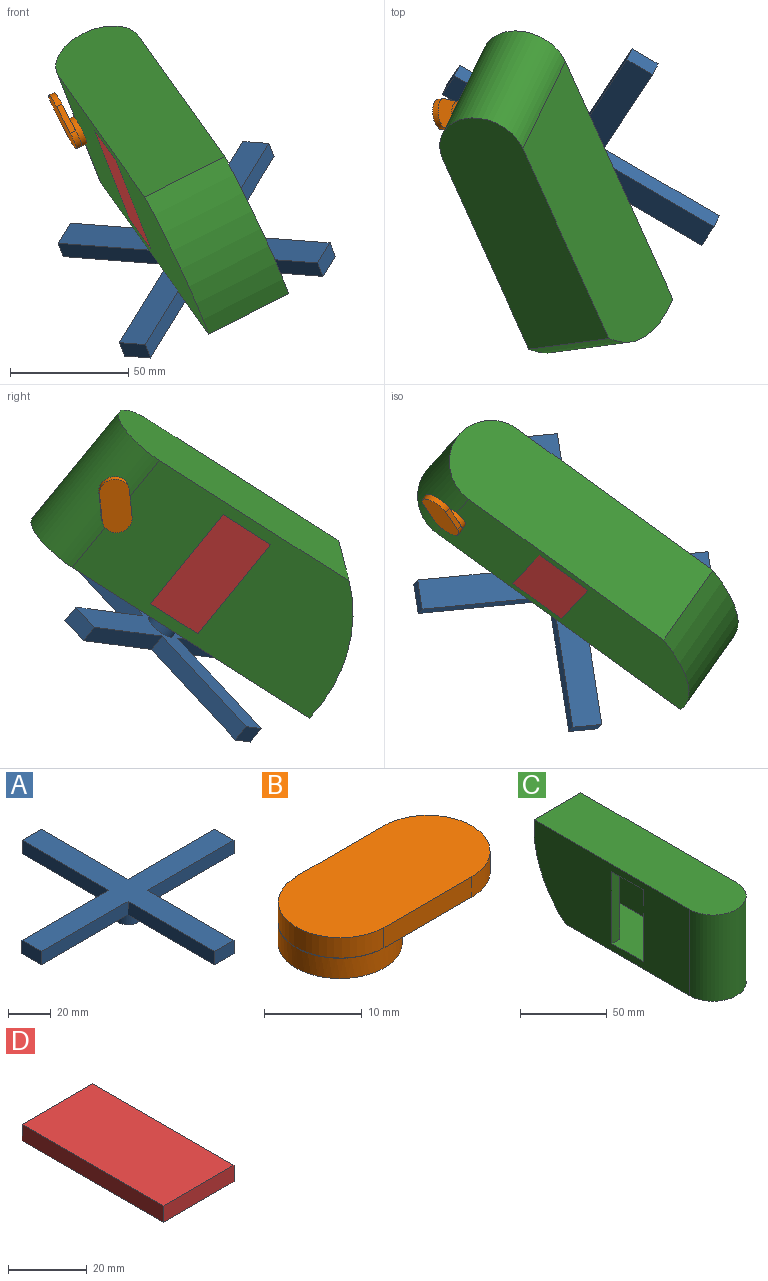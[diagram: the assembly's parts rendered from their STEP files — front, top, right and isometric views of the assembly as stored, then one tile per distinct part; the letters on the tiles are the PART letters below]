
ASSEMBLY  parts=4 mates=3
PART A: 16 faces, bbox 127x127x15.2 mm
  f0: plane 57.15x7.62mm, normal (0,-1,0), area 435.5mm2, adj f1,f11,f12,f13
  f1: plane 57.15x7.62mm, normal (-1,0,0), area 435.5mm2, adj f0,f2,f12,f13
  f2: plane 12.7x7.62mm, normal (0,-1,0), area 96.8mm2, adj f1,f3,f12,f13
  f3: plane 57.15x7.62mm, normal (1,0,0), area 435.5mm2, adj f2,f4,f12,f13
  f4: plane 57.15x7.62mm, normal (0,-1,0), area 435.5mm2, adj f3,f5,f12,f13
  f5: plane 12.7x7.62mm, normal (1,0,0), area 96.8mm2, adj f4,f6,f12,f13
  f6: plane 57.15x7.62mm, normal (0,1,0), area 435.5mm2, adj f5,f7,f12,f13
  f7: plane 57.15x7.62mm, normal (1,0,0), area 435.5mm2, adj f6,f8,f12,f13
  f8: plane 12.7x7.62mm, normal (0,1,0), area 96.8mm2, adj f7,f9,f12,f13
  f9: plane 57.15x7.62mm, normal (-1,0,0), area 435.5mm2, adj f8,f10,f12,f13
  f10: plane 57.15x7.62mm, normal (0,1,0), area 435.5mm2, adj f9,f11,f12,f13
  f11: plane 12.7x7.62mm, normal (-1,0,0), area 96.8mm2, adj f0,f10,f12,f13
  f12: plane 127x127mm, normal (0,0,1), area 3064.5mm2, adj f0,f1,f2,f3,f4,f5,f6,f7
  f13: plane 127x127mm, normal (0,0,-1), area 2937.8mm2, adj f0,f1,f2,f3,f4,f5,f6,f7
  f14: cylinder r=6.35mm len=12.7mm, axis (0,0,1), area 304mm2, adj f13,f15
  f15: plane 12.7x12.7mm, normal (0,0,-1), area 126.7mm2, adj f14
PART B: 10 faces, bbox 25.4x12.7x5.1 mm
  f0: cylinder r=6.35mm len=12.7mm, axis (0,0,-1), area 101.3mm2, adj f1,f2,f3
  f1: plane 12.7x6.35mm, normal (0,0,1), area 0.8mm2, adj f0,f7
  f2: plane 12.7x12.7mm, normal (0,0,-1), area 126.7mm2, adj f0
  f3: plane 19.07x12.75mm, normal (0,0,-1), area 162.4mm2, adj f0,f4,f5,f6,f8
  f4: cylinder r=6.37mm len=12.75mm, axis (0,0,-1), area 50.9mm2, adj f3,f5,f8,f9
  f5: plane 12.7x2.54mm, normal (0,1,0), area 32.3mm2, adj f3,f4,f6,f9
  f6: plane 2.54x0.05mm, normal (-1,0,0), area 0.1mm2, adj f3,f5,f7,f9
  f7: cylinder r=6.35mm len=12.7mm, axis (0,0,-1), area 50.4mm2, adj f1,f6,f8,f9
  f8: plane 12.7x2.54mm, normal (0,-1,0), area 32.3mm2, adj f3,f4,f7,f9
  f9: plane 25.36x12.75mm, normal (0,0,1), area 288.3mm2, adj f4,f5,f6,f7,f8
PART C: 15 faces, bbox 38.1x146.3x61 mm
  f0: plane 127.22x60.96mm, normal (1,0,0), area 7321.1mm2, adj f10,f12,f13,f14
  f1: plane 127.22x60.96mm, normal (-1,0,0), area 6030.8mm2, adj f2,f8,f9,f10,f11,f12,f13,f14
  f2: plane 50.8x6.35mm, normal (0,-1,0), area 322.6mm2, adj f1,f3,f9,f11
  f3: plane 50.8x31.75mm, normal (1,0,0), area 1612.9mm2, adj f2,f4,f9,f11
  f4: plane 50.8x25.4mm, normal (0,-1,0), area 1290.3mm2, adj f3,f5,f9,f11
  f5: plane 88.9x50.8mm, normal (-1,0,0), area 4516.1mm2, adj f4,f6,f9,f11
  f6: plane 50.8x25.4mm, normal (0,1,0), area 1290.3mm2, adj f5,f7,f9,f11
  f7: plane 50.8x31.75mm, normal (1,0,0), area 1612.9mm2, adj f6,f8,f9,f11
  f8: plane 50.8x6.35mm, normal (0,1,0), area 322.6mm2, adj f1,f7,f9,f11
  f9: plane 88.9x31.75mm, normal (0,0,1), area 2419.4mm2, adj f1,f2,f3,f4,f5,f6,f7,f8
  f10: plane 120.65x38.1mm, normal (0,0,-1), area 4441mm2, adj f0,f1,f13,f14
  f11: plane 88.9x31.75mm, normal (0,0,-1), area 2419.3mm2, adj f1,f2,f3,f4,f5,f6,f7,f8
  f12: plane 146.05x38.1mm, normal (0,0,1), area 5408.7mm2, adj f0,f1,f13,f14
  f13: cylinder r=19.05mm len=60.96mm, axis (0,0,-1), area 3648.3mm2, adj f0,f1,f10,f12
  f14: cylinder r=72.66mm len=60.96mm, axis (1,0,0), area 2611.9mm2, adj f0,f1,f10,f12
PART D: 6 faces, bbox 25.4x50.8x5.1 mm
  f0: plane 25.4x5.08mm, normal (0,-1,0), area 129mm2, adj f1,f3,f4,f5
  f1: plane 50.8x5.08mm, normal (1,0,0), area 258.1mm2, adj f0,f2,f4,f5
  f2: plane 25.4x5.08mm, normal (0,1,0), area 129mm2, adj f1,f3,f4,f5
  f3: plane 50.8x5.08mm, normal (-1,0,0), area 258.1mm2, adj f0,f2,f4,f5
  f4: plane 50.8x25.4mm, normal (0,0,1), area 1290.3mm2, adj f0,f1,f2,f3
  f5: plane 50.8x25.4mm, normal (0,0,-1), area 1290.3mm2, adj f0,f1,f2,f3
PLACE A rot(axis=(0.25,0.9,0.36),172.7deg) t=(5.42,-35.53,66.57)mm
PLACE B rot(axis=(-0.01,-1,0.09),117.3deg) t=(-42.66,-16.66,114.3)mm
PLACE C rot(axis=(-0.97,-0.13,-0.21),145.2deg) t=(-15.11,-69.82,116.19)mm fixed
PLACE D rot(axis=(0.48,0.29,0.83),139.2deg) t=(-24.52,-56.71,88.84)mm
MATE revolute C.f12 <-> A.f14  axis (0.29,0.6,-0.74) through (3.18,-40.13,72.22)mm
MATE planar C.f1 <-> D.f5  axis (-0.89,-0.12,-0.45) through (-19.98,-66.72,82.48)mm
MATE revolute B.f0 <-> C.f1  axis (0.89,0.12,0.45) through (-42.66,-16.66,114.3)mm
